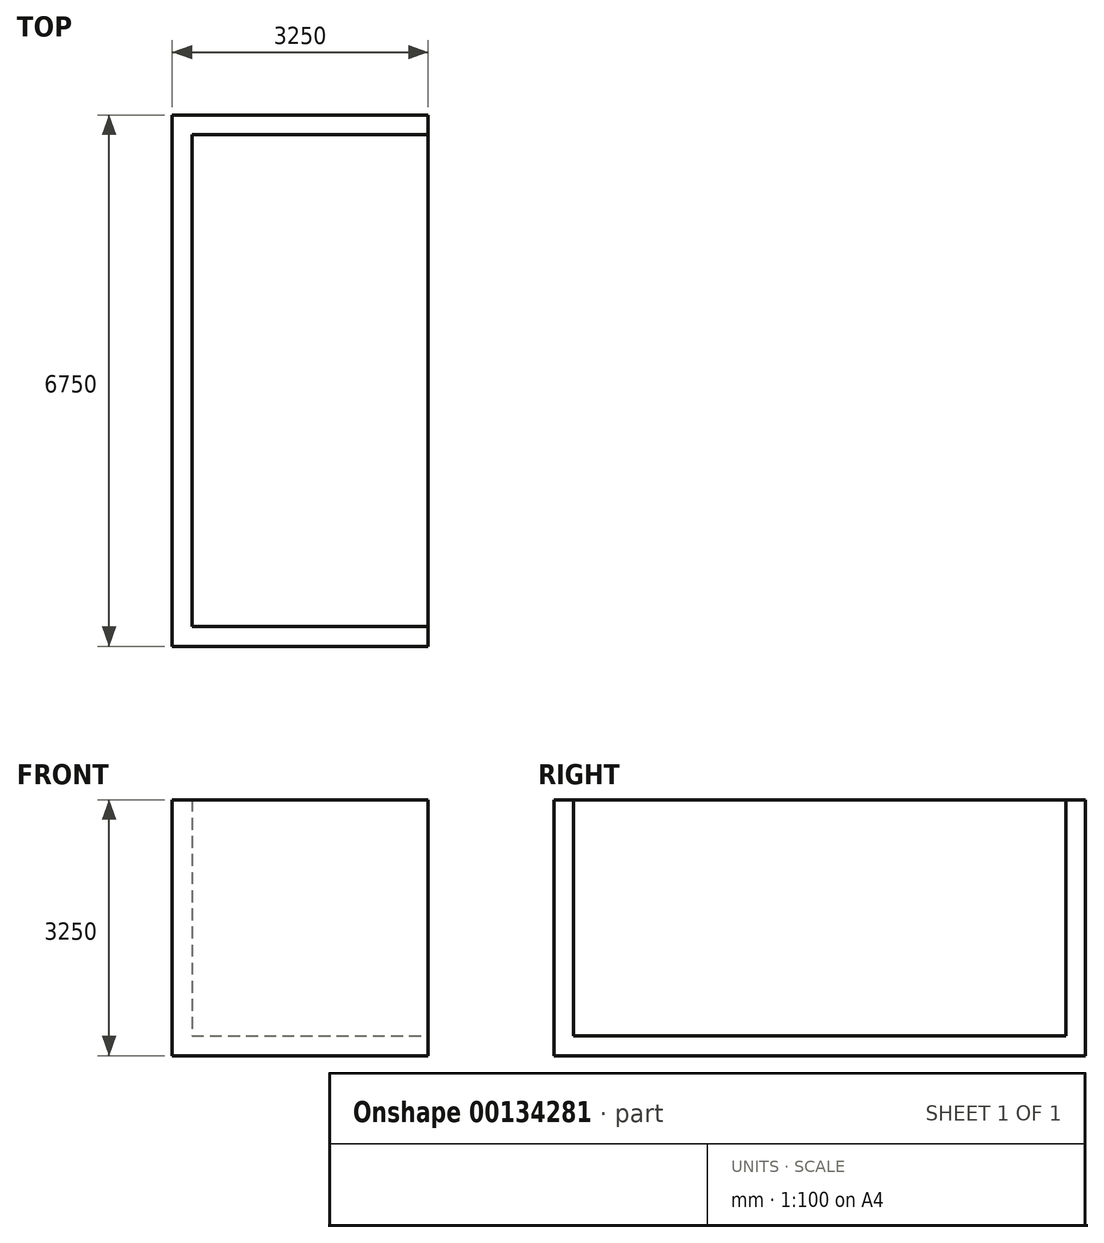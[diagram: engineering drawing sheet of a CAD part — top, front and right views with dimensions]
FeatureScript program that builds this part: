
annotation { "Feature Type Name" : "Feature", "Feature Type Description" : "" }
export const myFeature = defineFeature(function(context is Context, id is Id, definition is map)
    precondition{}
    {
        {
            var Q0;
            Q0=qCreatedBy(makeId("Top.planeOp"),FACE);
            var sketch = newSketch(context, id + "F0", { "sketchPlane" : qUnion([Q0])});
            skLineSegment(sketch, "E0.bottom", {"start": v(0, 0) * mm, "end": v(3000, 0) * mm});
            skLineSegment(sketch, "E0.top", {"start": v(0, 6250) * mm, "end": v(3000, 6250) * mm});
            skLineSegment(sketch, "E0.left", {"start": v(0, 0) * mm, "end": v(0, 6250) * mm});
            skLineSegment(sketch, "E0.right", {"start": v(3000, 0) * mm, "end": v(3000, 6250) * mm});
            skSolve(sketch);
        }
        {
            var Q0;
            Q0 = qSketchRegion(id + "F0", true);
            extrude(context, id + "F1", {"entities" : qUnion([Q0]), "depth" : 3000 * mm});
        }
        {
            var Q0;
            Q0=makeQuery(id+"F1.opExtrude","CAP_FACE",FACE,{"disambiguationData":[OSD([sQuery(id+"F0.wireOp",EDGE,"E0.bottom"),sQuery(id+"F0.wireOp",EDGE,"E0.top"),sQuery(id+"F0.wireOp",EDGE,"E0.left"),sQuery(id+"F0.wireOp",EDGE,"E0.right")])],"isStart":false});
            var Q1;
            Q1=makeQuery(id+"F1.opExtrude","SWEPT_FACE",FACE,{"disambiguationData":[OSD([sQuery(id+"F0.wireOp",EDGE,"E0.right")])]});
            var Q2;
            Q2=makeQuery(id+"F1.opExtrude","SWEPT_BODY",BODY,{"disambiguationData":[OSD([sQuery(id+"F0.wireOp",EDGE,"E0.bottom"),sQuery(id+"F0.wireOp",EDGE,"E0.top"),sQuery(id+"F0.wireOp",EDGE,"E0.left"),sQuery(id+"F0.wireOp",EDGE,"E0.right")])]});
            shell(context, id + "F2", {"entities" : qUnion([Q0, Q1]), "parts" : qUnion([Q2]), "thickness" : 250 * mm, "oppositeDirection" : true});
        }
    });
